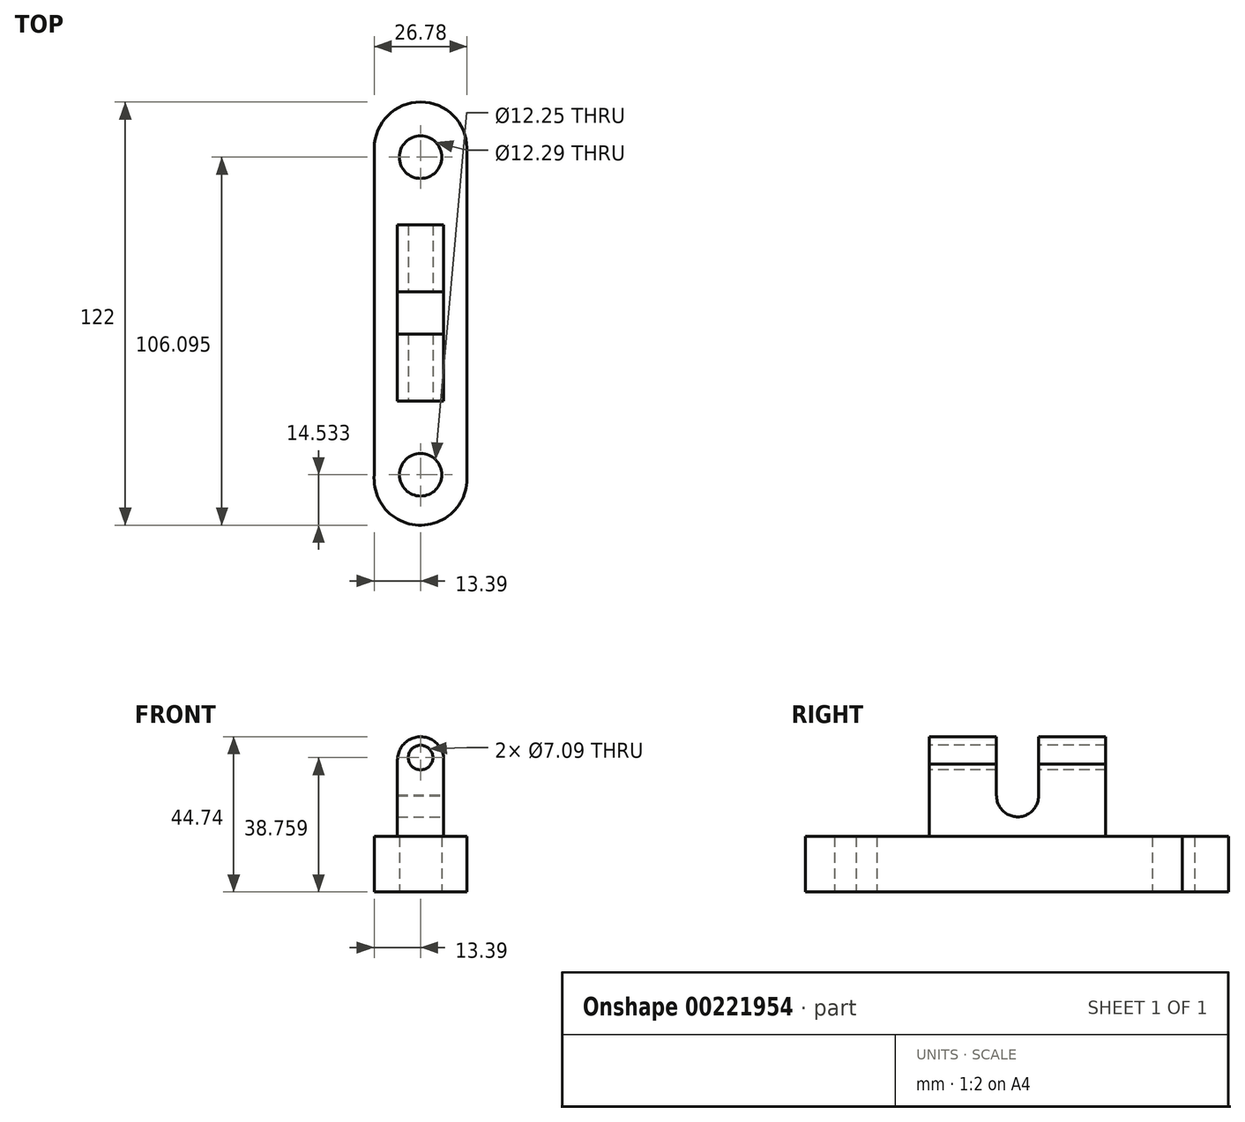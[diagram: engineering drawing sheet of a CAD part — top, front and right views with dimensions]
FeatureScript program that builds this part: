
annotation { "Feature Type Name" : "Feature", "Feature Type Description" : "" }
export const myFeature = defineFeature(function(context is Context, id is Id, definition is map)
    precondition{}
    {
        {
            var Q0;
            Q0=qCreatedBy(makeId("Top.planeOp"),FACE);
            var sketch = newSketch(context, id + "F0", { "sketchPlane" : qUnion([Q0])});
            skCircle(sketch, "E0", {"center": v(0, 47.5) * mm, "radius": 13.34 * mm});
            skCircle(sketch, "E1", {"center": v(0, -47.78) * mm, "radius": 13.39 * mm});
            skLineSegment(sketch, "E2", {"start": v(-13.34, 47.5) * mm, "end": v(-13.34, -47.78) * mm});
            skLineSegment(sketch, "E3", {"start": v(-13.34, -47.78) * mm, "end": v(13.39, -47.78) * mm});
            skLineSegment(sketch, "E4", {"start": v(13.39, -47.78) * mm, "end": v(13.39, 47.5) * mm});
            skLineSegment(sketch, "E5", {"start": v(13.39, 47.5) * mm, "end": v(-13.34, 47.5) * mm});
            skSolve(sketch);
        }
        {
            var Q0;
            Q0 = qSketchRegion(id + "F0", true);
            extrude(context, id + "F1", {"entities" : qUnion([Q0]), "depth" : 16 * mm});
        }
        {
            var Q0;
            Q0=qCreatedBy(makeId("Top.planeOp"),FACE);
            var sketch = newSketch(context, id + "F2", { "sketchPlane" : qUnion([Q0])});
            skCircle(sketch, "E6", {"center": v(0, 44.93) * mm, "radius": 6.14 * mm});
            skCircle(sketch, "E7", {"center": v(0, -46.64) * mm, "radius": 6.12 * mm});
            skSolve(sketch);
        }
        {
            var Q0;
            Q0 = qSketchRegion(id + "F2", true);
            extrude(context, id + "F3", {"entities" : qUnion([Q0]), "operationType" : NewBodyOperationType.REMOVE, "endBound" : BoundingType.THROUGH_ALL, "depth" : 43.94 * mm});
        }
        {
            var Q0;
            Q0=qCreatedBy(makeId("Front.planeOp"),FACE);
            var sketch = newSketch(context, id + "F4", { "sketchPlane" : qUnion([Q0])});
            skCircle(sketch, "E8", {"center": v(0, 38.08) * mm, "radius": 6.66 * mm});
            skLineSegment(sketch, "E9", {"start": v(-6.66, 38.08) * mm, "end": v(-6.66, 2.7) * mm});
            skLineSegment(sketch, "E10", {"start": v(-6.66, 2.7) * mm, "end": v(6.56, 2.7) * mm});
            skLineSegment(sketch, "E11", {"start": v(6.56, 2.7) * mm, "end": v(6.56, 38.08) * mm});
            skLineSegment(sketch, "E12", {"start": v(6.56, 38.08) * mm, "end": v(-6.66, 38.08) * mm});
            skSolve(sketch);
        }
        {
            var Q0;
            Q0 = qSketchRegion(id + "F4", true);
            extrude(context, id + "F5", {"entities" : qUnion([Q0]), "operationType" : NewBodyOperationType.ADD, "depth" : 25.4 * mm, "hasSecondDirection" : true, "secondDirectionOppositeDirection" : true, "secondDirectionDepth" : 25.4 * mm});
        }
        {
            var Q0;
            Q0=qCreatedBy(makeId("Right.planeOp"),FACE);
            var sketch = newSketch(context, id + "F6", { "sketchPlane" : qUnion([Q0])});
            skCircle(sketch, "E13", {"center": v(0, 27.74) * mm, "radius": 6.06 * mm});
            skLineSegment(sketch, "E14", {"start": v(6.05, 27.49) * mm, "end": v(6.05, 48.87) * mm});
            skLineSegment(sketch, "E15", {"start": v(6.05, 48.87) * mm, "end": v(-6.09, 48.87) * mm});
            skLineSegment(sketch, "E16", {"start": v(-6.09, 48.87) * mm, "end": v(-6.09, 27.74) * mm});
            skLineSegment(sketch, "E17", {"start": v(-6.09, 27.74) * mm, "end": v(6.05, 27.49) * mm});
            skSolve(sketch);
        }
        {
            var Q0;
            Q0 = qSketchRegion(id + "F6", true);
            extrude(context, id + "F7", {"entities" : qUnion([Q0]), "operationType" : NewBodyOperationType.REMOVE, "oppositeDirection" : true, "depth" : 24.13 * mm, "hasSecondDirection" : true, "secondDirectionOppositeDirection" : false, "secondDirectionDepth" : 27.18 * mm});
        }
        {
            var Q0;
            Q0=qCreatedBy(makeId("Front.planeOp"),FACE);
            var sketch = newSketch(context, id + "F8", { "sketchPlane" : qUnion([Q0])});
            skCircle(sketch, "E18", {"center": v(0, 38.76) * mm, "radius": 3.54 * mm});
            skSolve(sketch);
        }
        {
            var Q0;
            Q0 = qSketchRegion(id + "F8", true);
            extrude(context, id + "F9", {"entities" : qUnion([Q0]), "operationType" : NewBodyOperationType.REMOVE, "oppositeDirection" : true, "depth" : 25.4 * mm, "hasSecondDirection" : true, "secondDirectionOppositeDirection" : false, "secondDirectionDepth" : 25.4 * mm});
        }
    });
